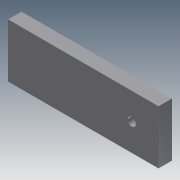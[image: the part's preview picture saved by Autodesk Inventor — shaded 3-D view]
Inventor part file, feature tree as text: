
AUTODESK INVENTOR PART (.ipt)
format: ipt  version: 2011 (Build 150239000, 239)  size: 92,160 bytes
history: native  units: in
note: dims shown in document units (in); Inventor stores cm internally (conversion verified against a paired STEP export)
features: extrude x4, sketch x4
ambient origin geometry x8: Origin, YZ Plane, XZ Plane, XY Plane, X Axis, Y Axis, Z Axis, Center Point
bodies: Solid1 (feature_tree)
feature tree (8):
  extrude  "Extrusion1"  Depth=1.0in
  extrude  "Extrusion2"  Depth=0.5in TaperAngle=0.0deg
  extrude  "Extrusion3"  Depth=0.156in
  extrude  "Extrusion4"  Depth=0.25in TaperAngle=0.0deg
  sketch  "Sketch1"  dims[d0=2.0482in d1=1.0in]
  sketch  "Sketch2"  dims[d2=0.25in d3=0.0in d4=0.5in d5=0.0in]
  sketch  "Sketch3"  dims[d6=0.5in d7=0.156in]
  sketch  "Sketch4"  dims[d8=0.5in d9=0.0in d10=0.25in d11=0.0in]
